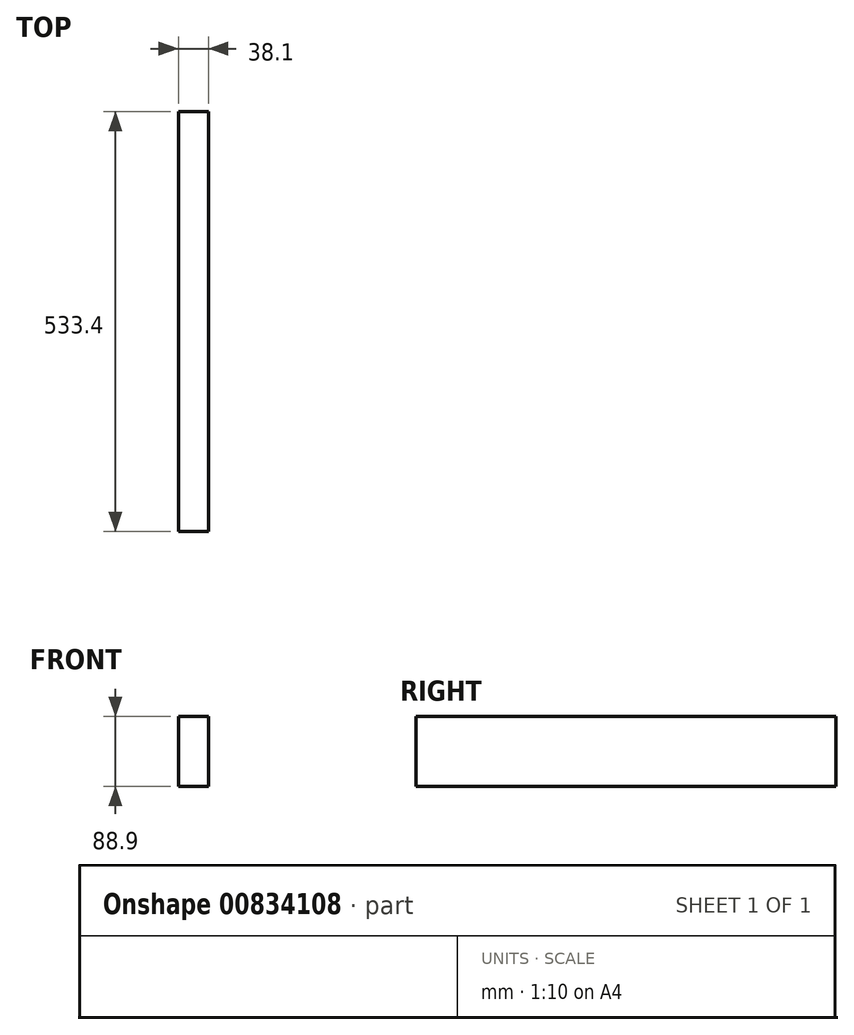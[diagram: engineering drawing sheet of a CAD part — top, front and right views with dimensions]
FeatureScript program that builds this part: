
annotation { "Feature Type Name" : "Feature", "Feature Type Description" : "" }
export const myFeature = defineFeature(function(context is Context, id is Id, definition is map)
    precondition{}
    {
        {
            var Q0;
            Q0=qCreatedBy(makeId("Front.planeOp"),FACE);
            var sketch = newSketch(context, id + "F0", { "sketchPlane" : qUnion([Q0])});
            skLineSegment(sketch, "E0.bottom", {"start": v(19.05, -44.45) * mm, "end": v(-19.05, -44.45) * mm});
            skLineSegment(sketch, "E0.top", {"start": v(19.05, 44.45) * mm, "end": v(-19.05, 44.45) * mm});
            skLineSegment(sketch, "E0.left", {"start": v(19.05, -44.45) * mm, "end": v(19.05, 44.45) * mm});
            skLineSegment(sketch, "E0.right", {"start": v(-19.05, -44.45) * mm, "end": v(-19.05, 44.45) * mm});
            skPoint(sketch, "E0.middle", {"position": v(0, 0) * mm});
            skSolve(sketch);
        }
        {
            var Q0;
            Q0=qSketchRegion(id+"F0",true);
            extrude(context, id + "F1", {"entities" : qUnion([Q0]), "endBound" : BoundingType.SYMMETRIC, "depth" : 533.4 * mm});
        }
    });
